# Revit family: Hager-PABLO-Flush_mounted-IP40-With_Cover-Without_DIN-Hosted-IT-it
name_source: partatom
category: Electrical Equipment
units: mm (PartAtom-declared; Revit-internal decimal feet)

## family parameters
Cut with Voids When Loaded = No
Host = Face
Maintain Annotation Orientation = Yes
Panel Configuration = Two Columns, Circuits Across
Part Type = Panelboard
Room Calculation Point = No
Round Connector Dimension = Use Diameter
Shared = No

## types (7) — shared parameters
BC_MODEL_ID = 1554423
BC_OBJECT_ID = 513913
BC_OBJECT_VERSION = #5
Code hager = ADD-EC000214_EU
EF000003 - Tipo di montaggio = Incassato
EF000024 - Resistente ai raggi UV = No
EF000116 - Numero RAL = 9016
EF000118 - Con piastra di montaggio = No
EF001062 - Esecuzione EMC = No
EF001088 - Possibilità di applicazione = No
EF001134 - Barra DIN = No
EF005474 - Grado di protezione (IP) = IP40
EF006244 - Coperchio/porta trasparente = No
EF006306 - Con serratura = No
EF015776 - Morsettiera di terra = No
EF015777 - Morsettiera neutra = No
EF015941 - Segnale di passaggio porta = No
ETIM class code = EC000214
ETIM class name = Small distribution board
HG000002-with door or cover-it = Yes
HG000003-Range-it = PABLO
HG000005-Thickness-it = 2 mm  [stored 0.00656168 ft]
HG000006-Flush mounted-it = Yes
HG000009-Double swing door-it = No
HG000010-Asymmetric doors-it = No
HG000011-Empty rows from bottom-it = No
HG000012-Door swing angle-it = 90.00°
HG000013-Door on the left-it = No
HG000014-Door on the right-it = Yes
HG000015-Clearance visibility-it = Yes
HG000016-Door 3D visibility-it = Yes
HG000017-Distance between poles-it = 18 mm  [stored 0.0590551 ft]
HG000060-RAL-number = 9016
HG000099-Onfly Template ID-it-IT = 507532
Manufacturer = Hager
Name = PABLO-Flush_mounted-IP40-With_Cover-Without_DIN-IT
Name BIM&CO = Electricity
Name hager = ADD_Enclosures_EC000214
Uniformat = Low Tension Service & Dist.
Uniformat code = D501001
zero-valued in all types: Default Elevation, EF001131 - Profondità interna, HG000001 - Numero di colonne, HG000007-Number of empty columns-it, HG000008-Number of empty rows-it

## per-type parameters (varying)
| type | BC_VARIANT_ID | EF000008 - Larghezza | EF000040 - Altezza | EF000049 - Profondità | EF000218 - Profondità di incasso | EF000266 - Numero di file | EF000332 - Altezza della parte incassata | EF000846 - Larghezza di montaggio | EF002950 - Numero moduli DIN | HG000004-Manufacturer reference-it | HGEF000266-Numero di file | HGEF0002950-Numero moduli DIN |
| PABLO-Flush_mounted_W169_H180_D99_4_Modular_Spacing-B04100 | 1179080 | 169 mm  [stored 0.554462 ft] | 180 mm  [stored 0.590551 ft] | 99 mm  [stored 0.324803 ft] | 74 mm  [stored 0.242782 ft] | 1 | 160 mm  [stored 0.524934 ft] | 169 mm  [stored 0.554462 ft] | 4 | B04100 | 1 | 4 |
| PABLO-Flush_mounted_W261_H225_D102_8_Modular_Spacing-B04101 | 1179081 | 261 mm | 225 mm  [stored 0.738189 ft] | 102 mm | 74 mm  [stored 0.242782 ft] | 1 | 205 mm  [stored 0.672572 ft] | 261 mm | 8 | B04101 | 1 | 8 |
| PABLO-Flush_mounted_W333_H275_D108_12_Modular_Spacing-B04102 | 1179082 | 333 mm  [stored 1.09252 ft] | 275 mm | 108 mm  [stored 0.354331 ft] | 77 mm  [stored 0.252625 ft] | 1 | 255 mm  [stored 0.836614 ft] | 333 mm  [stored 1.09252 ft] | 12 | B04102 | 1 | 12 |
| PABLO-Flush_mounted_W441_H300_D114_18_Modular_Spacing-B04103 | 1179083 | 441 mm  [stored 1.44685 ft] | 300 mm | 114 mm  [stored 0.374016 ft] | 77 mm  [stored 0.252625 ft] | 1 | 280 mm  [stored 0.918635 ft] | 441 mm  [stored 1.44685 ft] | 18 | B04103 | 1 | 18 |
| PABLO-Flush_mounted_W455_H650_D135_18_Modular_Spacing-B04106 | 1179084 | 455 mm | 650 mm  [stored 2.13255 ft] | 135 mm  [stored 0.442913 ft] | 77 mm  [stored 0.252625 ft] | 3 | 630 mm  [stored 2.06693 ft] | 455 mm | 18 | B04106 | 3 | 18 |
| PABLO-Flush_mounted_W205_H180_D101_6_Modular_Spacing-B04146 | 1179085 | 205 mm  [stored 0.672572 ft] | 180 mm  [stored 0.590551 ft] | 101 mm  [stored 0.331365 ft] | 74 mm  [stored 0.242782 ft] | 1 | 160 mm  [stored 0.524934 ft] | 205 mm  [stored 0.672572 ft] | 6 | B04146 | 1 | 6 |
| PABLO-Flush_mounted_W455_H850_D135_18_Modular_Spacing-B04147 | 1179086 | 455 mm | 850 mm  [stored 2.78871 ft] | 135 mm  [stored 0.442913 ft] | 98 mm  [stored 0.321522 ft] | 4 | 821 mm  [stored 2.69357 ft] | 455 mm | 18 | B04147 | 4 | 18 |

note: column(s) folded — value = type name in every type: Reference

note: [stored X ft] marks values corroborated as IEEE doubles in the binary element streams (Revit-internal decimal feet)

## geometry (parser evidence)
native form markers: Sweep x14
no freeform markers — native parametric forms only
